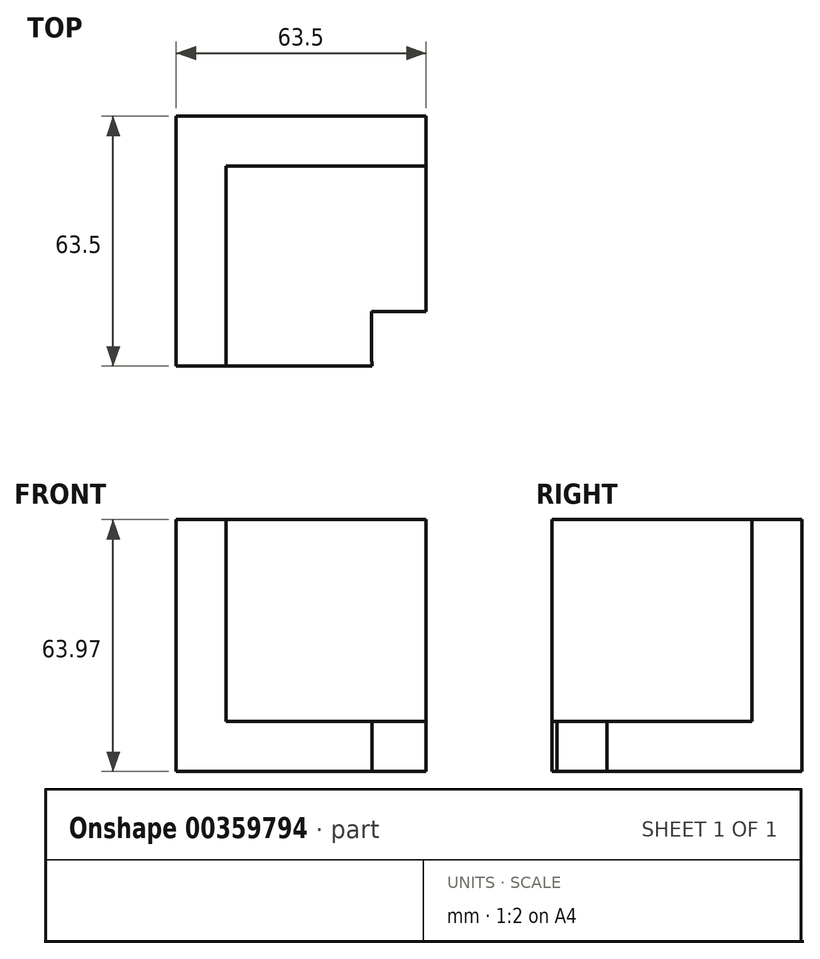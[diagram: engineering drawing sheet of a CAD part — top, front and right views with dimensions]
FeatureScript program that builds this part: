
annotation { "Feature Type Name" : "Feature", "Feature Type Description" : "" }
export const myFeature = defineFeature(function(context is Context, id is Id, definition is map)
    precondition{}
    {
        {
            var Q0;
            Q0=qCreatedBy(makeId("Front.planeOp"),FACE);
            var sketch = newSketch(context, id + "F0", { "sketchPlane" : qUnion([Q0])});
            skLineSegment(sketch, "E0.bottom", {"start": v(0, 0) * mm, "end": v(12.7, 0) * mm});
            skLineSegment(sketch, "E0.top", {"start": v(0, -63.5) * mm, "end": v(12.7, -63.5) * mm});
            skLineSegment(sketch, "E0.left", {"start": v(0, 0) * mm, "end": v(0, -63.5) * mm});
            skLineSegment(sketch, "E0.right", {"start": v(12.7, 0) * mm, "end": v(12.7, -63.5) * mm});
            skSolve(sketch);
        }
        {
            var Q0;
            Q0 = qSketchRegion(id + "F0", true);
            extrude(context, id + "F1", {"entities" : qUnion([Q0]), "depth" : 63.5 * mm});
        }
        {
            var Q0;
            Q0=qCreatedBy(makeId("Front.planeOp"),FACE);
            var sketch = newSketch(context, id + "F2", { "sketchPlane" : qUnion([Q0])});
            skLineSegment(sketch, "E1.bottom", {"start": v(0, 0) * mm, "end": v(63.5, 0) * mm});
            skLineSegment(sketch, "E1.top", {"start": v(0, -63.5) * mm, "end": v(63.5, -63.5) * mm});
            skLineSegment(sketch, "E1.left", {"start": v(0, 0) * mm, "end": v(0, -63.5) * mm});
            skLineSegment(sketch, "E1.right", {"start": v(63.5, 0) * mm, "end": v(63.5, -63.5) * mm});
            skSolve(sketch);
        }
        {
            var Q0;
            Q0 = qSketchRegion(id + "F2", true);
            extrude(context, id + "F3", {"entities" : qUnion([Q0]), "operationType" : NewBodyOperationType.ADD, "depth" : 12.7 * mm});
        }
        {
            var Q0;
            Q0=qCreatedBy(makeId("Front.planeOp"),FACE);
            var sketch = newSketch(context, id + "F4", { "sketchPlane" : qUnion([Q0])});
            skLineSegment(sketch, "E2.bottom", {"start": v(0, -63.97) * mm, "end": v(63.5, -63.97) * mm});
            skLineSegment(sketch, "E2.top", {"start": v(0, -51.27) * mm, "end": v(63.5, -51.27) * mm});
            skLineSegment(sketch, "E2.left", {"start": v(0, -63.97) * mm, "end": v(0, -51.27) * mm});
            skLineSegment(sketch, "E2.right", {"start": v(63.5, -63.97) * mm, "end": v(63.5, -51.27) * mm});
            skSolve(sketch);
        }
        {
            var Q0;
            Q0 = qSketchRegion(id + "F4", true);
            extrude(context, id + "F5", {"entities" : qUnion([Q0]), "operationType" : NewBodyOperationType.ADD, "depth" : 63.5 * mm});
        }
        {
            var Q0;
            Q0=makeQuery(id+"F5.opExtrude","SWEPT_FACE",FACE,{"disambiguationData":[OSD([sQuery(id+"F4.wireOp",EDGE,"E2.top")])]});
            var sketch = newSketch(context, id + "F6", { "sketchPlane" : qUnion([Q0])});
            skSolve(sketch);
        }
        {
            var Q0;
            {var subQ0=sQuery(id+"F4.wireOp",EDGE,"E2.top");Q0=makeQuery(id+"F6.imprint","IMPRINT",FACE,{"disambiguationData":[TD([[makeQuery(id+"F6.imprint","IMPRINT",EDGE,{"derivedFrom":makeQuery(id+"F5.opExtrude","CAP_EDGE",EDGE,{"disambiguationData":[OSD([subQ0])],"isStart":false})}),1.0]])]});}
            var sketch = newSketch(context, id + "F7", { "sketchPlane" : qUnion([Q0])});
            skLineSegment(sketch, "E3.bottom", {"start": v(62.32, -62.31) * mm, "end": v(49.62, -62.31) * mm});
            skLineSegment(sketch, "E3.top", {"start": v(62.32, -49.61) * mm, "end": v(49.62, -49.61) * mm});
            skLineSegment(sketch, "E3.left", {"start": v(62.32, -62.31) * mm, "end": v(62.32, -49.61) * mm});
            skLineSegment(sketch, "E3.right", {"start": v(49.62, -62.31) * mm, "end": v(49.62, -49.61) * mm});
            skSolve(sketch);
        }
        {
            var Q0;
            Q0 = qSketchRegion(id + "F7", true);
            extrude(context, id + "F8", {"entities" : qUnion([Q0]), "operationType" : NewBodyOperationType.REMOVE, "endBound" : BoundingType.THROUGH_ALL, "oppositeDirection" : true, "depth" : 25.4 * mm});
        }
        {
            var Q0;
            {var subQ0=sQuery(id+"F4.wireOp",EDGE,"E2.top");Q0=makeQuery(id+"F6.imprint","IMPRINT",FACE,{"disambiguationData":[TD([[makeQuery(id+"F6.imprint","IMPRINT",EDGE,{"derivedFrom":makeQuery(id+"F5.opExtrude","CAP_EDGE",EDGE,{"disambiguationData":[OSD([subQ0])],"isStart":false})}),1.0]])]});}
            var sketch = newSketch(context, id + "F9", { "sketchPlane" : qUnion([Q0])});
            skLineSegment(sketch, "E4.bottom", {"start": v(49.72, -49.62) * mm, "end": v(67.42, -49.62) * mm});
            skLineSegment(sketch, "E4.top", {"start": v(49.72, -66.6) * mm, "end": v(67.42, -66.6) * mm});
            skLineSegment(sketch, "E4.left", {"start": v(49.72, -49.62) * mm, "end": v(49.72, -66.6) * mm});
            skLineSegment(sketch, "E4.right", {"start": v(67.42, -49.62) * mm, "end": v(67.42, -66.6) * mm});
            skSolve(sketch);
        }
        {
            var Q0;
            Q0 = qSketchRegion(id + "F9", true);
            extrude(context, id + "F10", {"entities" : qUnion([Q0]), "operationType" : NewBodyOperationType.REMOVE, "oppositeDirection" : true, "depth" : 25.4 * mm});
        }
    });
